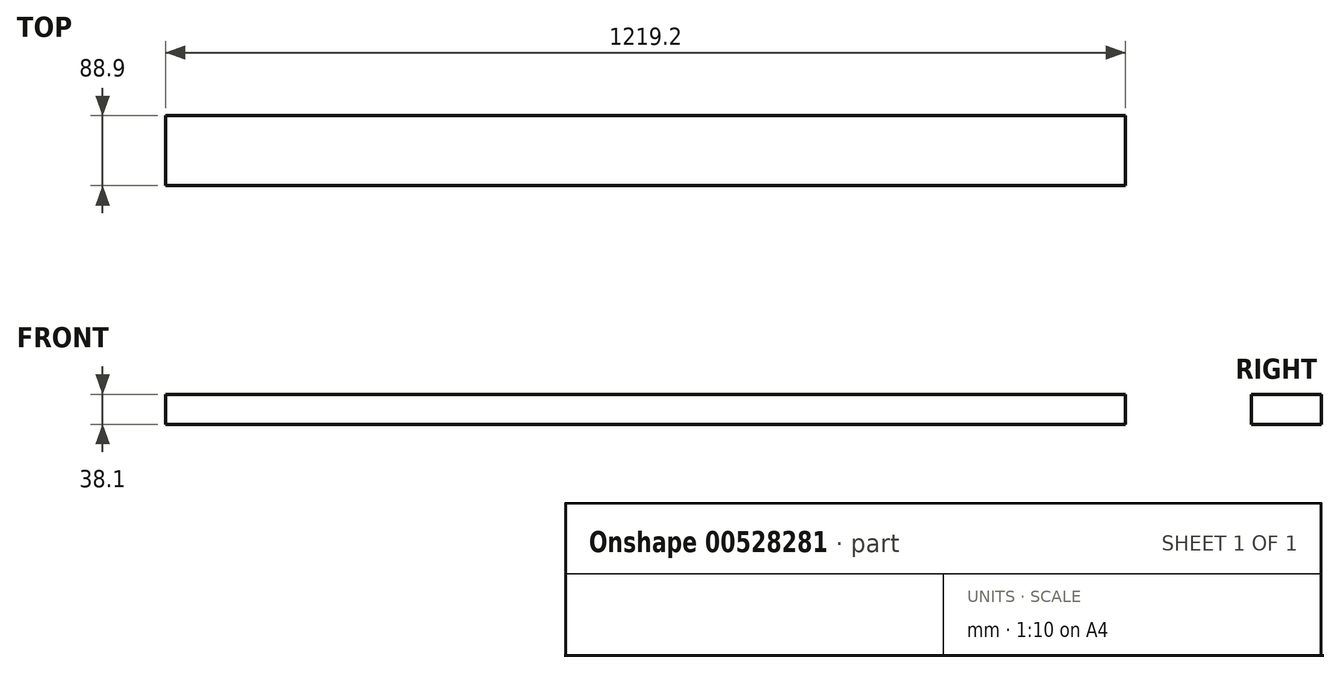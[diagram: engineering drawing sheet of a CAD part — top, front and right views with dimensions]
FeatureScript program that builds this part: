
annotation { "Feature Type Name" : "Feature", "Feature Type Description" : "" }
export const myFeature = defineFeature(function(context is Context, id is Id, definition is map)
    precondition{}
    {
        {
            var Q0;
            Q0=qCreatedBy(makeId("Front.planeOp"),FACE);
            var sketch = newSketch(context, id + "F0", { "sketchPlane" : qUnion([Q0])});
            skLineSegment(sketch, "E0.bottom", {"start": v(-171.12, -7) * mm, "end": v(1048.08, -7) * mm});
            skLineSegment(sketch, "E0.top", {"start": v(-171.12, -45.1) * mm, "end": v(1048.08, -45.1) * mm});
            skLineSegment(sketch, "E0.left", {"start": v(-171.12, -7) * mm, "end": v(-171.12, -45.1) * mm});
            skLineSegment(sketch, "E0.right", {"start": v(1048.08, -7) * mm, "end": v(1048.08, -45.1) * mm});
            skSolve(sketch);
        }
        {
            var Q0;
            Q0 = qSketchRegion(id + "F0", true);
            extrude(context, id + "F1", {"entities" : qUnion([Q0]), "depth" : 88.9 * mm, "offsetDistance" : 25.4 * mm});
        }
    });
